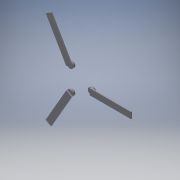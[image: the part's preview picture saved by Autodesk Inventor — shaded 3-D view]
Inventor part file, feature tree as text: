
AUTODESK INVENTOR PART (.ipt)
format: ipt  version: 2019 (Build 230136000, 136)  size: 120,320 bytes
history: native  units: in
note: dims shown in document units (in); Inventor stores cm internally (conversion verified against a paired STEP export)
features: reference x4, sketch x2, extrude x2, other x2, plane x1, pattern_circular x1
ambient origin geometry x8: Origin, YZ Plane, XZ Plane, XY Plane, X Axis, Y Axis, Z Axis, Center Point
bodies: Solid1 (feature_tree)
feature tree (12):
  sketch  "Sketch1"  dims[d0=1.0in d1=0.0in d2=3.7in]
  plane  "Work Plane1"
  extrude  "Extrusion1"  Depth=3.7in
  extrude  "Extrusion2"  Depth=0.1in TaperAngle=360.0deg
  pattern_circular  "Circular Pattern1"  [2 undecoded]
  reference  "Reference1"
  reference  "Reference2"
  reference  "Reference3"
  sketch  "Sketch2"  dims[d4=0.1in d5=0.0in d6=1.1811in d7=360.0deg]
  reference  "Reference4"
  other  "Assembly15"
  other  "Cutter:1"
note: 2 required parameter values undecoded (feature->parameter linkage not recoverable at this tier; creation-order binding heuristic only, values carry confidence <= 0.55)
